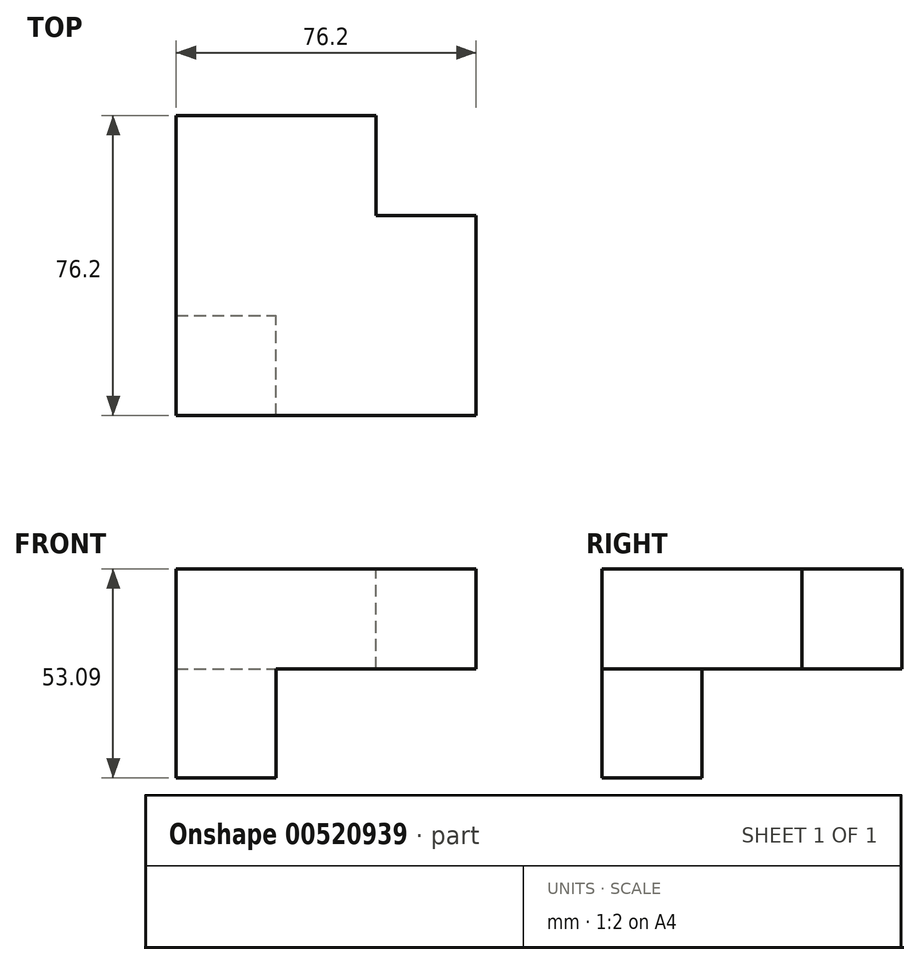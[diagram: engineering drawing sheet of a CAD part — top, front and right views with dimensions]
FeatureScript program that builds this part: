
annotation { "Feature Type Name" : "Feature", "Feature Type Description" : "" }
export const myFeature = defineFeature(function(context is Context, id is Id, definition is map)
    precondition{}
    {
        {
            var Q0;
            Q0=qCreatedBy(makeId("Top.planeOp"),FACE);
            var sketch = newSketch(context, id + "F0", { "sketchPlane" : qUnion([Q0])});
            skLineSegment(sketch, "E0.bottom", {"start": v(0, 0) * mm, "end": v(76.2, 0) * mm});
            skLineSegment(sketch, "E0.top", {"start": v(0, 76.2) * mm, "end": v(76.2, 76.2) * mm});
            skLineSegment(sketch, "E0.left", {"start": v(0, 0) * mm, "end": v(0, 76.2) * mm});
            skLineSegment(sketch, "E0.right", {"start": v(76.2, 0) * mm, "end": v(76.2, 76.2) * mm});
            skSolve(sketch);
        }
        {
            var Q0;
            Q0 = qSketchRegion(id + "F0", true);
            extrude(context, id + "F1", {"entities" : qUnion([Q0]), "depth" : 25.4 * mm, "offsetDistance" : 25.4 * mm});
        }
        {
            var Q0;
            Q0=makeQuery(id+"F1.opExtrude","CAP_FACE",FACE,{"disambiguationData":[OSD([sQuery(id+"F0.wireOp",EDGE,"E0.bottom"),sQuery(id+"F0.wireOp",EDGE,"E0.top"),sQuery(id+"F0.wireOp",EDGE,"E0.left"),sQuery(id+"F0.wireOp",EDGE,"E0.right")])],"isStart":false});
            var sketch = newSketch(context, id + "F2", { "sketchPlane" : qUnion([Q0])});
            skLineSegment(sketch, "E1.bottom", {"start": v(76.2, 76.2) * mm, "end": v(50.8, 76.2) * mm});
            skLineSegment(sketch, "E1.top", {"start": v(76.2, 50.8) * mm, "end": v(50.8, 50.8) * mm});
            skLineSegment(sketch, "E1.left", {"start": v(76.2, 76.2) * mm, "end": v(76.2, 50.8) * mm});
            skLineSegment(sketch, "E1.right", {"start": v(50.8, 76.2) * mm, "end": v(50.8, 50.8) * mm});
            skSolve(sketch);
        }
        {
            var Q0;
            Q0=makeQuery(id+"F2.imprint","IMPRINT",FACE,{"disambiguationData":[TD([[makeQuery(id+"F2.imprint","IMPRINT",EDGE,{"derivedFrom":sQuery(id+"F2.wireOp",EDGE,"E1.bottom")}),-1.0]])]});
            extrude(context, id + "F3", {"entities" : qUnion([Q0]), "operationType" : NewBodyOperationType.REMOVE, "oppositeDirection" : true, "depth" : 25.4 * mm, "offsetDistance" : 25.4 * mm});
        }
        {
            var Q0;
            Q0=qCreatedBy(makeId("Top.planeOp"),FACE);
            var sketch = newSketch(context, id + "F4", { "sketchPlane" : qUnion([Q0])});
            skLineSegment(sketch, "E2.bottom", {"start": v(0, 0) * mm, "end": v(25.4, 0) * mm});
            skLineSegment(sketch, "E2.top", {"start": v(0, 25.4) * mm, "end": v(25.4, 25.4) * mm});
            skLineSegment(sketch, "E2.left", {"start": v(0, 0) * mm, "end": v(0, 25.4) * mm});
            skLineSegment(sketch, "E2.right", {"start": v(25.4, 0) * mm, "end": v(25.4, 25.4) * mm});
            skSolve(sketch);
        }
        {
            var Q0;
            Q0=makeQuery(id+"F4.imprint","IMPRINT",FACE,{"disambiguationData":[TD([[makeQuery(id+"F4.imprint","IMPRINT",EDGE,{"derivedFrom":sQuery(id+"F4.wireOp",EDGE,"E2.bottom")}),1.0]])]});
            extrude(context, id + "F5", {"entities" : qUnion([Q0]), "operationType" : NewBodyOperationType.ADD, "oppositeDirection" : true, "depth" : 27.7 * mm, "offsetDistance" : 25.4 * mm});
        }
    });
